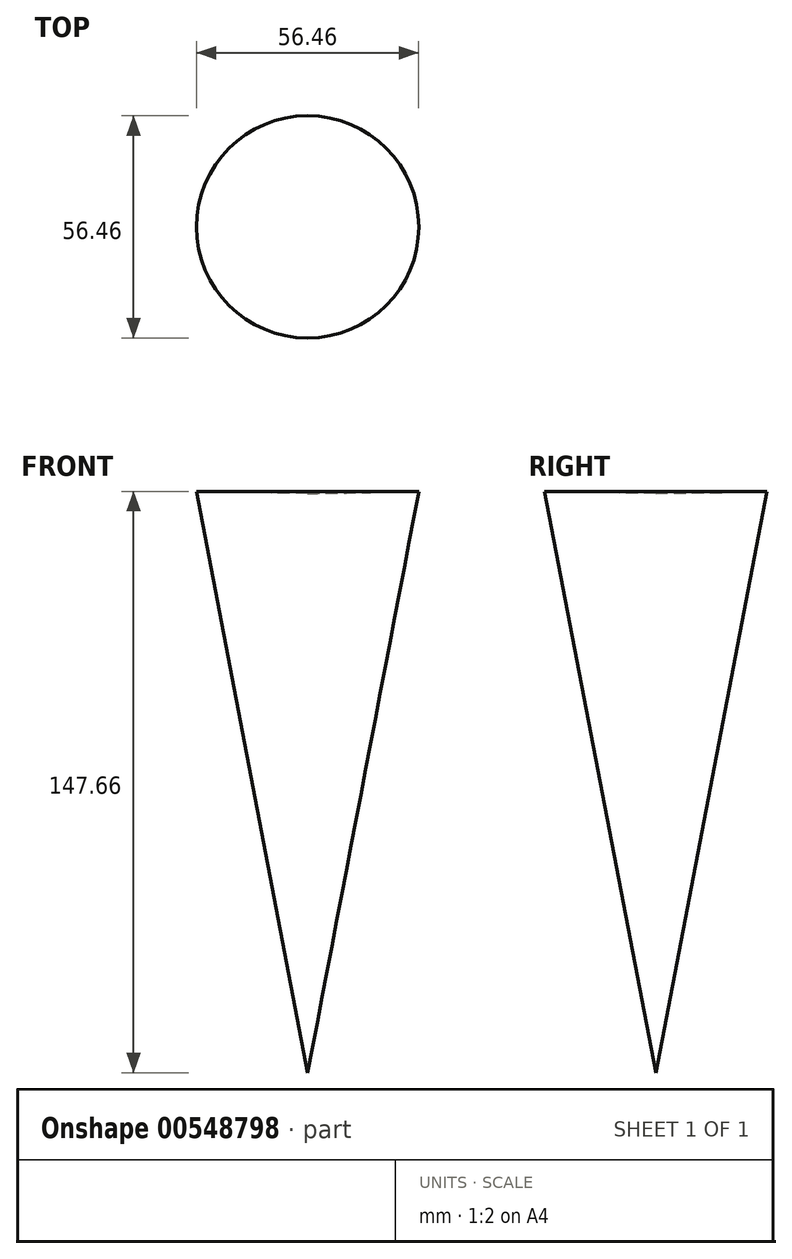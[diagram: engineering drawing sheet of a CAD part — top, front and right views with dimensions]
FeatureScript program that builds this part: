
annotation { "Feature Type Name" : "Feature", "Feature Type Description" : "" }
export const myFeature = defineFeature(function(context is Context, id is Id, definition is map)
    precondition{}
    {
        {
            var Q0;
            Q0=qCreatedBy(makeId("Front.planeOp"),FACE);
            var sketch = newSketch(context, id + "F0", { "sketchPlane" : qUnion([Q0])});
            skLineSegment(sketch, "E0", {"start": v(28.23, 72.89) * mm, "end": v(0, -74.77) * mm});
            skLineSegment(sketch, "E1", {"start": v(0, -74.77) * mm, "end": v(0, 72.39) * mm});
            skLineSegment(sketch, "E2", {"start": v(0, 72.39) * mm, "end": v(28.23, 72.89) * mm});
            skPoint(sketch, "E3", {"position": v(9.24, -26.42) * mm});
            skSolve(sketch);
        }
        {
            var Q0;
            Q0=makeQuery(id+"F0.imprint","IMPRINT",FACE,{"disambiguationData":[TD([[makeQuery(id+"F0.imprint","IMPRINT",EDGE,{"derivedFrom":sQuery(id+"F0.wireOp",EDGE,"E0")}),-1.0]])]});
            var Q1;
            Q1=sQuery(id+"F0.wireOp",EDGE,"E1");
            revolve(context, id + "F1", {"entities" : qUnion([Q0]), "axis" : qUnion([Q1]), "revolveType" : RevolveType.FULL});
        }
    });
